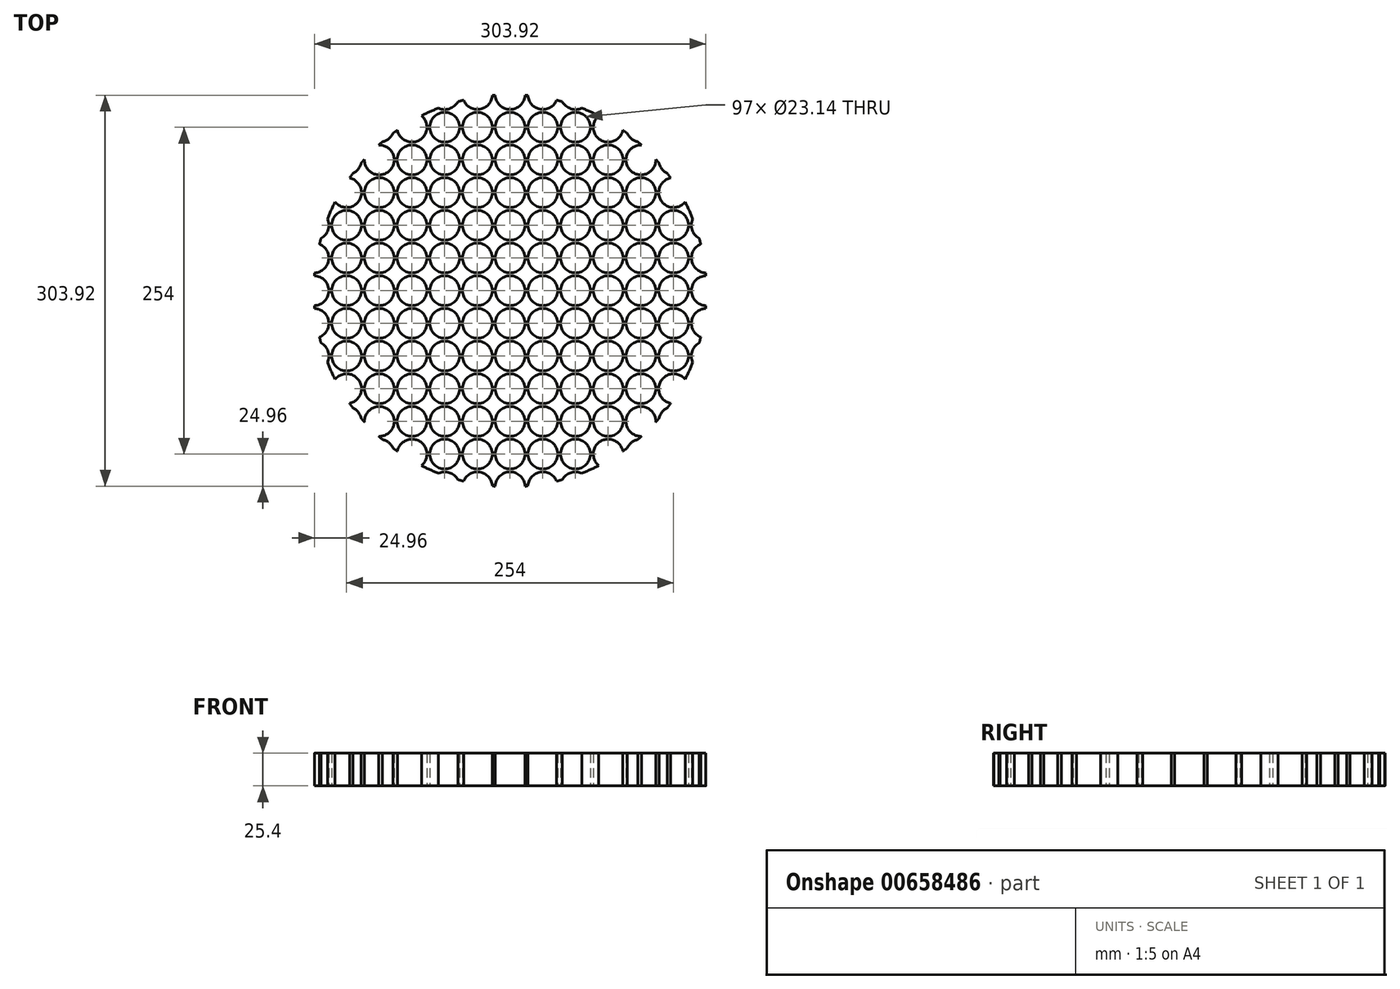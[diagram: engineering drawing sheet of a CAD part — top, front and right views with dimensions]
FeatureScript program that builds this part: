
annotation { "Feature Type Name" : "Feature", "Feature Type Description" : "" }
export const myFeature = defineFeature(function(context is Context, id is Id, definition is map)
    precondition{}
    {
        {
            var Q0;
            Q0=qCreatedBy(makeId("Top.planeOp"),FACE);
            var sketch = newSketch(context, id + "F0", { "sketchPlane" : qUnion([Q0])});
            skCircle(sketch, "E0", {"center": v(0, 0) * mm, "radius": 152.4 * mm});
            skCircle(sketch, "E1", {"center": v(-152.4, -152.4) * mm, "radius": 11.57 * mm});
            skCircle(sketch, "E2.0.1.0", {"center": v(-152.4, -127) * mm, "radius": 11.57 * mm});
            skCircle(sketch, "E2.0.2.0", {"center": v(-152.4, -101.6) * mm, "radius": 11.57 * mm});
            skCircle(sketch, "E2.0.3.0", {"center": v(-152.4, -76.2) * mm, "radius": 11.57 * mm});
            skCircle(sketch, "E2.0.4.0", {"center": v(-152.4, -50.8) * mm, "radius": 11.57 * mm});
            skCircle(sketch, "E2.0.5.0", {"center": v(-152.4, -25.4) * mm, "radius": 11.57 * mm});
            skCircle(sketch, "E2.0.6.0", {"center": v(-152.4, 0) * mm, "radius": 11.57 * mm});
            skCircle(sketch, "E2.0.7.0", {"center": v(-152.4, 25.4) * mm, "radius": 11.57 * mm});
            skCircle(sketch, "E2.0.8.0", {"center": v(-152.4, 50.8) * mm, "radius": 11.57 * mm});
            skCircle(sketch, "E2.0.9.0", {"center": v(-152.4, 76.2) * mm, "radius": 11.57 * mm});
            skCircle(sketch, "E2.0.10.0", {"center": v(-152.4, 101.6) * mm, "radius": 11.57 * mm});
            skCircle(sketch, "E2.0.11.0", {"center": v(-152.4, 127) * mm, "radius": 11.57 * mm});
            skCircle(sketch, "E2.1.0.0", {"center": v(-127, -152.4) * mm, "radius": 11.57 * mm});
            skCircle(sketch, "E2.1.1.0", {"center": v(-127, -127) * mm, "radius": 11.57 * mm});
            skCircle(sketch, "E2.1.2.0", {"center": v(-127, -101.6) * mm, "radius": 11.57 * mm});
            skCircle(sketch, "E2.1.3.0", {"center": v(-127, -76.2) * mm, "radius": 11.57 * mm});
            skCircle(sketch, "E2.1.4.0", {"center": v(-127, -50.8) * mm, "radius": 11.57 * mm});
            skCircle(sketch, "E2.1.5.0", {"center": v(-127, -25.4) * mm, "radius": 11.57 * mm});
            skCircle(sketch, "E2.1.6.0", {"center": v(-127, 0) * mm, "radius": 11.57 * mm});
            skCircle(sketch, "E2.1.7.0", {"center": v(-127, 25.4) * mm, "radius": 11.57 * mm});
            skCircle(sketch, "E2.1.8.0", {"center": v(-127, 50.8) * mm, "radius": 11.57 * mm});
            skCircle(sketch, "E2.1.9.0", {"center": v(-127, 76.2) * mm, "radius": 11.57 * mm});
            skCircle(sketch, "E2.1.10.0", {"center": v(-127, 101.6) * mm, "radius": 11.57 * mm});
            skCircle(sketch, "E2.1.11.0", {"center": v(-127, 127) * mm, "radius": 11.57 * mm});
            skCircle(sketch, "E2.2.0.0", {"center": v(-101.6, -152.4) * mm, "radius": 11.57 * mm});
            skCircle(sketch, "E2.2.1.0", {"center": v(-101.6, -127) * mm, "radius": 11.57 * mm});
            skCircle(sketch, "E2.2.2.0", {"center": v(-101.6, -101.6) * mm, "radius": 11.57 * mm});
            skCircle(sketch, "E2.2.3.0", {"center": v(-101.6, -76.2) * mm, "radius": 11.57 * mm});
            skCircle(sketch, "E2.2.4.0", {"center": v(-101.6, -50.8) * mm, "radius": 11.57 * mm});
            skCircle(sketch, "E2.2.5.0", {"center": v(-101.6, -25.4) * mm, "radius": 11.57 * mm});
            skCircle(sketch, "E2.2.6.0", {"center": v(-101.6, 0) * mm, "radius": 11.57 * mm});
            skCircle(sketch, "E2.2.7.0", {"center": v(-101.6, 25.4) * mm, "radius": 11.57 * mm});
            skCircle(sketch, "E2.2.8.0", {"center": v(-101.6, 50.8) * mm, "radius": 11.57 * mm});
            skCircle(sketch, "E2.2.9.0", {"center": v(-101.6, 76.2) * mm, "radius": 11.57 * mm});
            skCircle(sketch, "E2.2.10.0", {"center": v(-101.6, 101.6) * mm, "radius": 11.57 * mm});
            skCircle(sketch, "E2.2.11.0", {"center": v(-101.6, 127) * mm, "radius": 11.57 * mm});
            skCircle(sketch, "E2.3.0.0", {"center": v(-76.2, -152.4) * mm, "radius": 11.57 * mm});
            skCircle(sketch, "E2.3.1.0", {"center": v(-76.2, -127) * mm, "radius": 11.57 * mm});
            skCircle(sketch, "E2.3.2.0", {"center": v(-76.2, -101.6) * mm, "radius": 11.57 * mm});
            skCircle(sketch, "E2.3.3.0", {"center": v(-76.2, -76.2) * mm, "radius": 11.57 * mm});
            skCircle(sketch, "E2.3.4.0", {"center": v(-76.2, -50.8) * mm, "radius": 11.57 * mm});
            skCircle(sketch, "E2.3.5.0", {"center": v(-76.2, -25.4) * mm, "radius": 11.57 * mm});
            skCircle(sketch, "E2.3.6.0", {"center": v(-76.2, 0) * mm, "radius": 11.57 * mm});
            skCircle(sketch, "E2.3.7.0", {"center": v(-76.2, 25.4) * mm, "radius": 11.57 * mm});
            skCircle(sketch, "E2.3.8.0", {"center": v(-76.2, 50.8) * mm, "radius": 11.57 * mm});
            skCircle(sketch, "E2.3.9.0", {"center": v(-76.2, 76.2) * mm, "radius": 11.57 * mm});
            skCircle(sketch, "E2.3.10.0", {"center": v(-76.2, 101.6) * mm, "radius": 11.57 * mm});
            skCircle(sketch, "E2.3.11.0", {"center": v(-76.2, 127) * mm, "radius": 11.57 * mm});
            skCircle(sketch, "E2.4.0.0", {"center": v(-50.8, -152.4) * mm, "radius": 11.57 * mm});
            skCircle(sketch, "E2.4.1.0", {"center": v(-50.8, -127) * mm, "radius": 11.57 * mm});
            skCircle(sketch, "E2.4.2.0", {"center": v(-50.8, -101.6) * mm, "radius": 11.57 * mm});
            skCircle(sketch, "E2.4.3.0", {"center": v(-50.8, -76.2) * mm, "radius": 11.57 * mm});
            skCircle(sketch, "E2.4.4.0", {"center": v(-50.8, -50.8) * mm, "radius": 11.57 * mm});
            skCircle(sketch, "E2.4.5.0", {"center": v(-50.8, -25.4) * mm, "radius": 11.57 * mm});
            skCircle(sketch, "E2.4.6.0", {"center": v(-50.8, 0) * mm, "radius": 11.57 * mm});
            skCircle(sketch, "E2.4.7.0", {"center": v(-50.8, 25.4) * mm, "radius": 11.57 * mm});
            skCircle(sketch, "E2.4.8.0", {"center": v(-50.8, 50.8) * mm, "radius": 11.57 * mm});
            skCircle(sketch, "E2.4.9.0", {"center": v(-50.8, 76.2) * mm, "radius": 11.57 * mm});
            skCircle(sketch, "E2.4.10.0", {"center": v(-50.8, 101.6) * mm, "radius": 11.57 * mm});
            skCircle(sketch, "E2.4.11.0", {"center": v(-50.8, 127) * mm, "radius": 11.57 * mm});
            skCircle(sketch, "E2.5.0.0", {"center": v(-25.4, -152.4) * mm, "radius": 11.57 * mm});
            skCircle(sketch, "E2.5.1.0", {"center": v(-25.4, -127) * mm, "radius": 11.57 * mm});
            skCircle(sketch, "E2.5.2.0", {"center": v(-25.4, -101.6) * mm, "radius": 11.57 * mm});
            skCircle(sketch, "E2.5.3.0", {"center": v(-25.4, -76.2) * mm, "radius": 11.57 * mm});
            skCircle(sketch, "E2.5.4.0", {"center": v(-25.4, -50.8) * mm, "radius": 11.57 * mm});
            skCircle(sketch, "E2.5.5.0", {"center": v(-25.4, -25.4) * mm, "radius": 11.57 * mm});
            skCircle(sketch, "E2.5.6.0", {"center": v(-25.4, 0) * mm, "radius": 11.57 * mm});
            skCircle(sketch, "E2.5.7.0", {"center": v(-25.4, 25.4) * mm, "radius": 11.57 * mm});
            skCircle(sketch, "E2.5.8.0", {"center": v(-25.4, 50.8) * mm, "radius": 11.57 * mm});
            skCircle(sketch, "E2.5.9.0", {"center": v(-25.4, 76.2) * mm, "radius": 11.57 * mm});
            skCircle(sketch, "E2.5.10.0", {"center": v(-25.4, 101.6) * mm, "radius": 11.57 * mm});
            skCircle(sketch, "E2.5.11.0", {"center": v(-25.4, 127) * mm, "radius": 11.57 * mm});
            skCircle(sketch, "E2.6.0.0", {"center": v(0, -152.4) * mm, "radius": 11.57 * mm});
            skCircle(sketch, "E2.6.1.0", {"center": v(0, -127) * mm, "radius": 11.57 * mm});
            skCircle(sketch, "E2.6.2.0", {"center": v(0, -101.6) * mm, "radius": 11.57 * mm});
            skCircle(sketch, "E2.6.3.0", {"center": v(0, -76.2) * mm, "radius": 11.57 * mm});
            skCircle(sketch, "E2.6.4.0", {"center": v(0, -50.8) * mm, "radius": 11.57 * mm});
            skCircle(sketch, "E2.6.5.0", {"center": v(0, -25.4) * mm, "radius": 11.57 * mm});
            skCircle(sketch, "E2.6.6.0", {"center": v(0, 0) * mm, "radius": 11.57 * mm});
            skCircle(sketch, "E2.6.7.0", {"center": v(0, 25.4) * mm, "radius": 11.57 * mm});
            skCircle(sketch, "E2.6.8.0", {"center": v(0, 50.8) * mm, "radius": 11.57 * mm});
            skCircle(sketch, "E2.6.9.0", {"center": v(0, 76.2) * mm, "radius": 11.57 * mm});
            skCircle(sketch, "E2.6.10.0", {"center": v(0, 101.6) * mm, "radius": 11.57 * mm});
            skCircle(sketch, "E2.6.11.0", {"center": v(0, 127) * mm, "radius": 11.57 * mm});
            skCircle(sketch, "E2.7.0.0", {"center": v(25.4, -152.4) * mm, "radius": 11.57 * mm});
            skCircle(sketch, "E2.7.1.0", {"center": v(25.4, -127) * mm, "radius": 11.57 * mm});
            skCircle(sketch, "E2.7.2.0", {"center": v(25.4, -101.6) * mm, "radius": 11.57 * mm});
            skCircle(sketch, "E2.7.3.0", {"center": v(25.4, -76.2) * mm, "radius": 11.57 * mm});
            skCircle(sketch, "E2.7.4.0", {"center": v(25.4, -50.8) * mm, "radius": 11.57 * mm});
            skCircle(sketch, "E2.7.5.0", {"center": v(25.4, -25.4) * mm, "radius": 11.57 * mm});
            skCircle(sketch, "E2.7.6.0", {"center": v(25.4, 0) * mm, "radius": 11.57 * mm});
            skCircle(sketch, "E2.7.7.0", {"center": v(25.4, 25.4) * mm, "radius": 11.57 * mm});
            skCircle(sketch, "E2.7.8.0", {"center": v(25.4, 50.8) * mm, "radius": 11.57 * mm});
            skCircle(sketch, "E2.7.9.0", {"center": v(25.4, 76.2) * mm, "radius": 11.57 * mm});
            skCircle(sketch, "E2.7.10.0", {"center": v(25.4, 101.6) * mm, "radius": 11.57 * mm});
            skCircle(sketch, "E2.7.11.0", {"center": v(25.4, 127) * mm, "radius": 11.57 * mm});
            skCircle(sketch, "E2.8.0.0", {"center": v(50.8, -152.4) * mm, "radius": 11.57 * mm});
            skCircle(sketch, "E2.8.1.0", {"center": v(50.8, -127) * mm, "radius": 11.57 * mm});
            skCircle(sketch, "E2.8.2.0", {"center": v(50.8, -101.6) * mm, "radius": 11.57 * mm});
            skCircle(sketch, "E2.8.3.0", {"center": v(50.8, -76.2) * mm, "radius": 11.57 * mm});
            skCircle(sketch, "E2.8.4.0", {"center": v(50.8, -50.8) * mm, "radius": 11.57 * mm});
            skCircle(sketch, "E2.8.5.0", {"center": v(50.8, -25.4) * mm, "radius": 11.57 * mm});
            skCircle(sketch, "E2.8.6.0", {"center": v(50.8, 0) * mm, "radius": 11.57 * mm});
            skCircle(sketch, "E2.8.7.0", {"center": v(50.8, 25.4) * mm, "radius": 11.57 * mm});
            skCircle(sketch, "E2.8.8.0", {"center": v(50.8, 50.8) * mm, "radius": 11.57 * mm});
            skCircle(sketch, "E2.8.9.0", {"center": v(50.8, 76.2) * mm, "radius": 11.57 * mm});
            skCircle(sketch, "E2.8.10.0", {"center": v(50.8, 101.6) * mm, "radius": 11.57 * mm});
            skCircle(sketch, "E2.8.11.0", {"center": v(50.8, 127) * mm, "radius": 11.57 * mm});
            skCircle(sketch, "E2.9.0.0", {"center": v(76.2, -152.4) * mm, "radius": 11.57 * mm});
            skCircle(sketch, "E2.9.1.0", {"center": v(76.2, -127) * mm, "radius": 11.57 * mm});
            skCircle(sketch, "E2.9.2.0", {"center": v(76.2, -101.6) * mm, "radius": 11.57 * mm});
            skCircle(sketch, "E2.9.3.0", {"center": v(76.2, -76.2) * mm, "radius": 11.57 * mm});
            skCircle(sketch, "E2.9.4.0", {"center": v(76.2, -50.8) * mm, "radius": 11.57 * mm});
            skCircle(sketch, "E2.9.5.0", {"center": v(76.2, -25.4) * mm, "radius": 11.57 * mm});
            skCircle(sketch, "E2.9.6.0", {"center": v(76.2, 0) * mm, "radius": 11.57 * mm});
            skCircle(sketch, "E2.9.7.0", {"center": v(76.2, 25.4) * mm, "radius": 11.57 * mm});
            skCircle(sketch, "E2.9.8.0", {"center": v(76.2, 50.8) * mm, "radius": 11.57 * mm});
            skCircle(sketch, "E2.9.9.0", {"center": v(76.2, 76.2) * mm, "radius": 11.57 * mm});
            skCircle(sketch, "E2.9.10.0", {"center": v(76.2, 101.6) * mm, "radius": 11.57 * mm});
            skCircle(sketch, "E2.9.11.0", {"center": v(76.2, 127) * mm, "radius": 11.57 * mm});
            skCircle(sketch, "E2.10.0.0", {"center": v(101.6, -152.4) * mm, "radius": 11.57 * mm});
            skCircle(sketch, "E2.10.1.0", {"center": v(101.6, -127) * mm, "radius": 11.57 * mm});
            skCircle(sketch, "E2.10.2.0", {"center": v(101.6, -101.6) * mm, "radius": 11.57 * mm});
            skCircle(sketch, "E2.10.3.0", {"center": v(101.6, -76.2) * mm, "radius": 11.57 * mm});
            skCircle(sketch, "E2.10.4.0", {"center": v(101.6, -50.8) * mm, "radius": 11.57 * mm});
            skCircle(sketch, "E2.10.5.0", {"center": v(101.6, -25.4) * mm, "radius": 11.57 * mm});
            skCircle(sketch, "E2.10.6.0", {"center": v(101.6, 0) * mm, "radius": 11.57 * mm});
            skCircle(sketch, "E2.10.7.0", {"center": v(101.6, 25.4) * mm, "radius": 11.57 * mm});
            skCircle(sketch, "E2.10.8.0", {"center": v(101.6, 50.8) * mm, "radius": 11.57 * mm});
            skCircle(sketch, "E2.10.9.0", {"center": v(101.6, 76.2) * mm, "radius": 11.57 * mm});
            skCircle(sketch, "E2.10.10.0", {"center": v(101.6, 101.6) * mm, "radius": 11.57 * mm});
            skCircle(sketch, "E2.10.11.0", {"center": v(101.6, 127) * mm, "radius": 11.57 * mm});
            skCircle(sketch, "E2.11.0.0", {"center": v(127, -152.4) * mm, "radius": 11.57 * mm});
            skCircle(sketch, "E2.11.1.0", {"center": v(127, -127) * mm, "radius": 11.57 * mm});
            skCircle(sketch, "E2.11.2.0", {"center": v(127, -101.6) * mm, "radius": 11.57 * mm});
            skCircle(sketch, "E2.11.3.0", {"center": v(127, -76.2) * mm, "radius": 11.57 * mm});
            skCircle(sketch, "E2.11.4.0", {"center": v(127, -50.8) * mm, "radius": 11.57 * mm});
            skCircle(sketch, "E2.11.5.0", {"center": v(127, -25.4) * mm, "radius": 11.57 * mm});
            skCircle(sketch, "E2.11.6.0", {"center": v(127, 0) * mm, "radius": 11.57 * mm});
            skCircle(sketch, "E2.11.7.0", {"center": v(127, 25.4) * mm, "radius": 11.57 * mm});
            skCircle(sketch, "E2.11.8.0", {"center": v(127, 50.8) * mm, "radius": 11.57 * mm});
            skCircle(sketch, "E2.11.9.0", {"center": v(127, 76.2) * mm, "radius": 11.57 * mm});
            skCircle(sketch, "E2.11.10.0", {"center": v(127, 101.6) * mm, "radius": 11.57 * mm});
            skCircle(sketch, "E2.11.11.0", {"center": v(127, 127) * mm, "radius": 11.57 * mm});
            skLineSegment(sketch, "E2.direction1", {"start": v(-152.4, -152.4) * mm, "end": v(-127, -152.4) * mm, "construction": true});
            skLineSegment(sketch, "E2.direction2", {"start": v(-152.4, -152.4) * mm, "end": v(-152.4, -127) * mm, "construction": true});
            skCircle(sketch, "E3.0.12.0", {"center": v(152.4, -152.4) * mm, "radius": 11.57 * mm});
            skCircle(sketch, "E3.0.12.1", {"center": v(152.4, -127) * mm, "radius": 11.57 * mm});
            skCircle(sketch, "E3.0.12.2", {"center": v(152.4, -101.6) * mm, "radius": 11.57 * mm});
            skCircle(sketch, "E3.0.12.3", {"center": v(152.4, -76.2) * mm, "radius": 11.57 * mm});
            skCircle(sketch, "E3.0.12.4", {"center": v(152.4, -50.8) * mm, "radius": 11.57 * mm});
            skCircle(sketch, "E3.0.12.5", {"center": v(152.4, -25.4) * mm, "radius": 11.57 * mm});
            skCircle(sketch, "E3.0.12.6", {"center": v(152.4, 0) * mm, "radius": 11.57 * mm});
            skCircle(sketch, "E3.0.12.7", {"center": v(152.4, 25.4) * mm, "radius": 11.57 * mm});
            skCircle(sketch, "E3.0.12.8", {"center": v(152.4, 50.8) * mm, "radius": 11.57 * mm});
            skCircle(sketch, "E3.0.12.9", {"center": v(152.4, 76.2) * mm, "radius": 11.57 * mm});
            skCircle(sketch, "E3.0.12.10", {"center": v(152.4, 101.6) * mm, "radius": 11.57 * mm});
            skCircle(sketch, "E3.0.12.11", {"center": v(152.4, 127) * mm, "radius": 11.57 * mm});
            skCircle(sketch, "E3.0.13.0", {"center": v(177.8, -152.4) * mm, "radius": 11.57 * mm});
            skCircle(sketch, "E3.0.13.1", {"center": v(177.8, -127) * mm, "radius": 11.57 * mm});
            skCircle(sketch, "E3.0.13.2", {"center": v(177.8, -101.6) * mm, "radius": 11.57 * mm});
            skCircle(sketch, "E3.0.13.3", {"center": v(177.8, -76.2) * mm, "radius": 11.57 * mm});
            skCircle(sketch, "E3.0.13.4", {"center": v(177.8, -50.8) * mm, "radius": 11.57 * mm});
            skCircle(sketch, "E3.0.13.5", {"center": v(177.8, -25.4) * mm, "radius": 11.57 * mm});
            skCircle(sketch, "E3.0.13.6", {"center": v(177.8, 0) * mm, "radius": 11.57 * mm});
            skCircle(sketch, "E3.0.13.7", {"center": v(177.8, 25.4) * mm, "radius": 11.57 * mm});
            skCircle(sketch, "E3.0.13.8", {"center": v(177.8, 50.8) * mm, "radius": 11.57 * mm});
            skCircle(sketch, "E3.0.13.9", {"center": v(177.8, 76.2) * mm, "radius": 11.57 * mm});
            skCircle(sketch, "E3.0.13.10", {"center": v(177.8, 101.6) * mm, "radius": 11.57 * mm});
            skCircle(sketch, "E3.0.13.11", {"center": v(177.8, 127) * mm, "radius": 11.57 * mm});
            skCircle(sketch, "E4.0.0.12", {"center": v(-152.4, 152.4) * mm, "radius": 11.57 * mm});
            skCircle(sketch, "E4.0.0.13", {"center": v(-152.4, 177.8) * mm, "radius": 11.57 * mm});
            skCircle(sketch, "E4.0.1.12", {"center": v(-127, 152.4) * mm, "radius": 11.57 * mm});
            skCircle(sketch, "E4.0.1.13", {"center": v(-127, 177.8) * mm, "radius": 11.57 * mm});
            skCircle(sketch, "E4.0.2.12", {"center": v(-101.6, 152.4) * mm, "radius": 11.57 * mm});
            skCircle(sketch, "E4.0.2.13", {"center": v(-101.6, 177.8) * mm, "radius": 11.57 * mm});
            skCircle(sketch, "E4.0.3.12", {"center": v(-76.2, 152.4) * mm, "radius": 11.57 * mm});
            skCircle(sketch, "E4.0.3.13", {"center": v(-76.2, 177.8) * mm, "radius": 11.57 * mm});
            skCircle(sketch, "E4.0.4.12", {"center": v(-50.8, 152.4) * mm, "radius": 11.57 * mm});
            skCircle(sketch, "E4.0.4.13", {"center": v(-50.8, 177.8) * mm, "radius": 11.57 * mm});
            skCircle(sketch, "E4.0.5.12", {"center": v(-25.4, 152.4) * mm, "radius": 11.57 * mm});
            skCircle(sketch, "E4.0.5.13", {"center": v(-25.4, 177.8) * mm, "radius": 11.57 * mm});
            skCircle(sketch, "E4.0.6.12", {"center": v(0, 152.4) * mm, "radius": 11.57 * mm});
            skCircle(sketch, "E4.0.6.13", {"center": v(0, 177.8) * mm, "radius": 11.57 * mm});
            skCircle(sketch, "E4.0.7.12", {"center": v(25.4, 152.4) * mm, "radius": 11.57 * mm});
            skCircle(sketch, "E4.0.7.13", {"center": v(25.4, 177.8) * mm, "radius": 11.57 * mm});
            skCircle(sketch, "E4.0.8.12", {"center": v(50.8, 152.4) * mm, "radius": 11.57 * mm});
            skCircle(sketch, "E4.0.8.13", {"center": v(50.8, 177.8) * mm, "radius": 11.57 * mm});
            skCircle(sketch, "E4.0.9.12", {"center": v(76.2, 152.4) * mm, "radius": 11.57 * mm});
            skCircle(sketch, "E4.0.9.13", {"center": v(76.2, 177.8) * mm, "radius": 11.57 * mm});
            skCircle(sketch, "E4.0.10.12", {"center": v(101.6, 152.4) * mm, "radius": 11.57 * mm});
            skCircle(sketch, "E4.0.10.13", {"center": v(101.6, 177.8) * mm, "radius": 11.57 * mm});
            skCircle(sketch, "E4.0.11.12", {"center": v(127, 152.4) * mm, "radius": 11.57 * mm});
            skCircle(sketch, "E4.0.11.13", {"center": v(127, 177.8) * mm, "radius": 11.57 * mm});
            skCircle(sketch, "E4.0.12.12", {"center": v(152.4, 152.4) * mm, "radius": 11.57 * mm});
            skCircle(sketch, "E4.0.12.13", {"center": v(152.4, 177.8) * mm, "radius": 11.57 * mm});
            skCircle(sketch, "E4.0.13.12", {"center": v(177.8, 152.4) * mm, "radius": 11.57 * mm});
            skCircle(sketch, "E4.0.13.13", {"center": v(177.8, 177.8) * mm, "radius": 11.57 * mm});
            skSolve(sketch);
        }
        {
            var Q0;
            Q0=makeQuery(id+"F0.imprint","IMPRINT",FACE,{"disambiguationData":[TD([[makeQuery(id+"F0.imprint","IMPRINT",EDGE,{"derivedFrom":sQuery(id+"F0.wireOp",EDGE,"E2.1.4.0")}),-1.0]])]});
            extrude(context, id + "F1", {"entities" : qUnion([Q0]), "depth" : 25.4 * mm, "offsetDistance" : 25.4 * mm});
        }
    });
